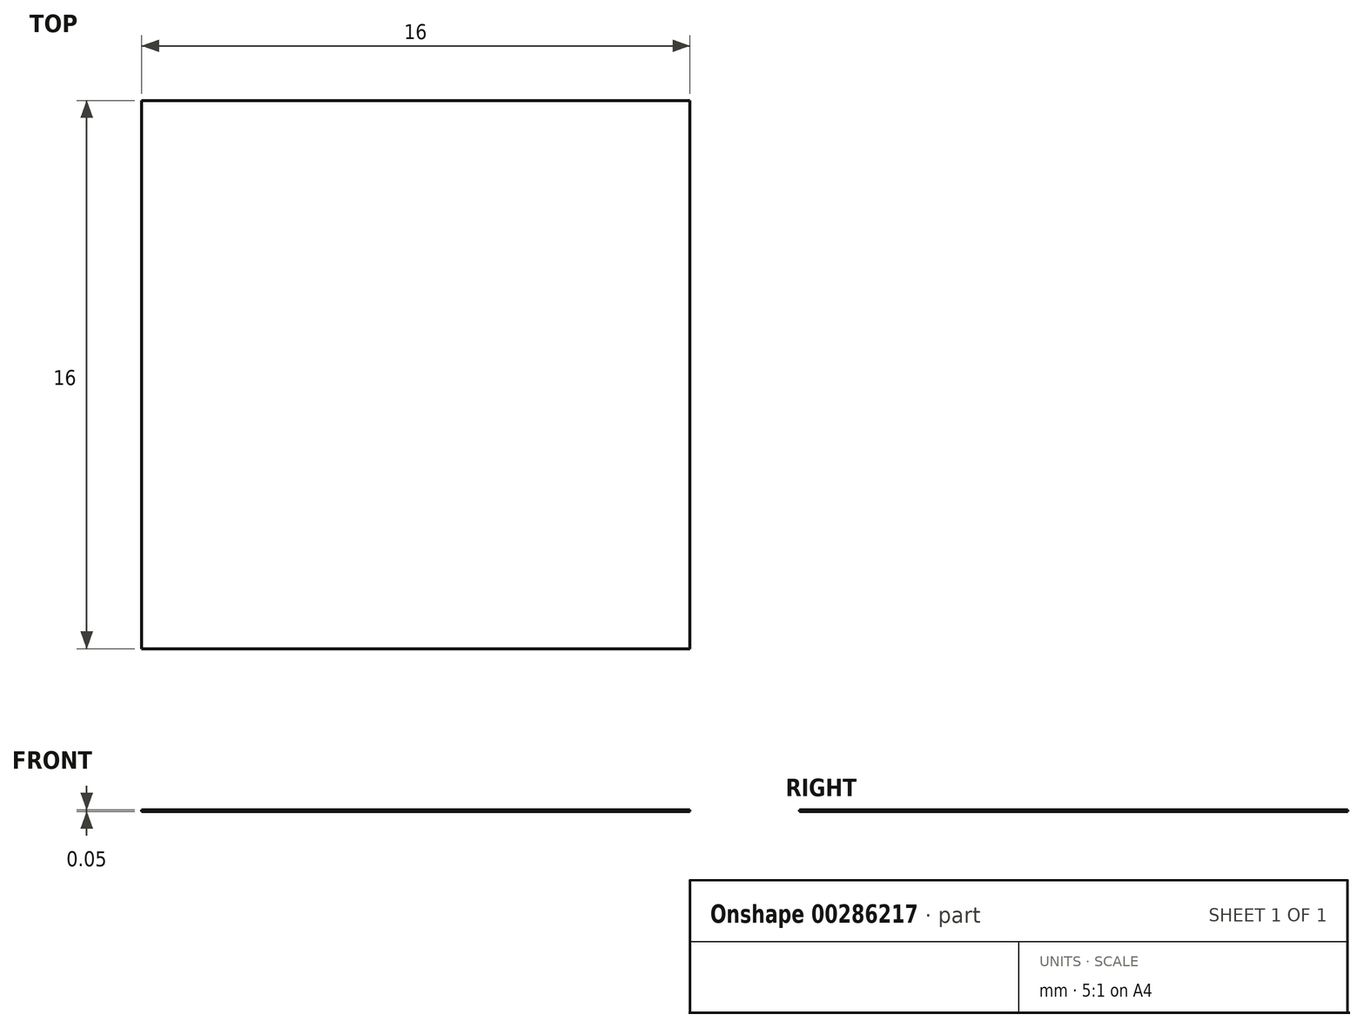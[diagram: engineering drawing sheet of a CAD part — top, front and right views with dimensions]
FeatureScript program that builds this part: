
annotation { "Feature Type Name" : "Feature", "Feature Type Description" : "" }
export const myFeature = defineFeature(function(context is Context, id is Id, definition is map)
    precondition{}
    {
        {
            var Q0;
            Q0=qCreatedBy(makeId("Top.planeOp"),FACE);
            var sketch = newSketch(context, id + "F0", { "sketchPlane" : qUnion([Q0])});
            skLineSegment(sketch, "E0.bottom", {"start": v(8, -8) * mm, "end": v(-8, -8) * mm});
            skLineSegment(sketch, "E0.top", {"start": v(8, 8) * mm, "end": v(-8, 8) * mm});
            skLineSegment(sketch, "E0.left", {"start": v(8, -8) * mm, "end": v(8, 8) * mm});
            skLineSegment(sketch, "E0.right", {"start": v(-8, -8) * mm, "end": v(-8, 8) * mm});
            skPoint(sketch, "E0.middle", {"position": v(0, 0) * mm});
            skSolve(sketch);
        }
        {
            var Q0;
            Q0 = qSketchRegion(id + "F0", true);
            extrude(context, id + "F1", {"entities" : qUnion([Q0]), "depth" : 0.05 * mm});
        }
    });
